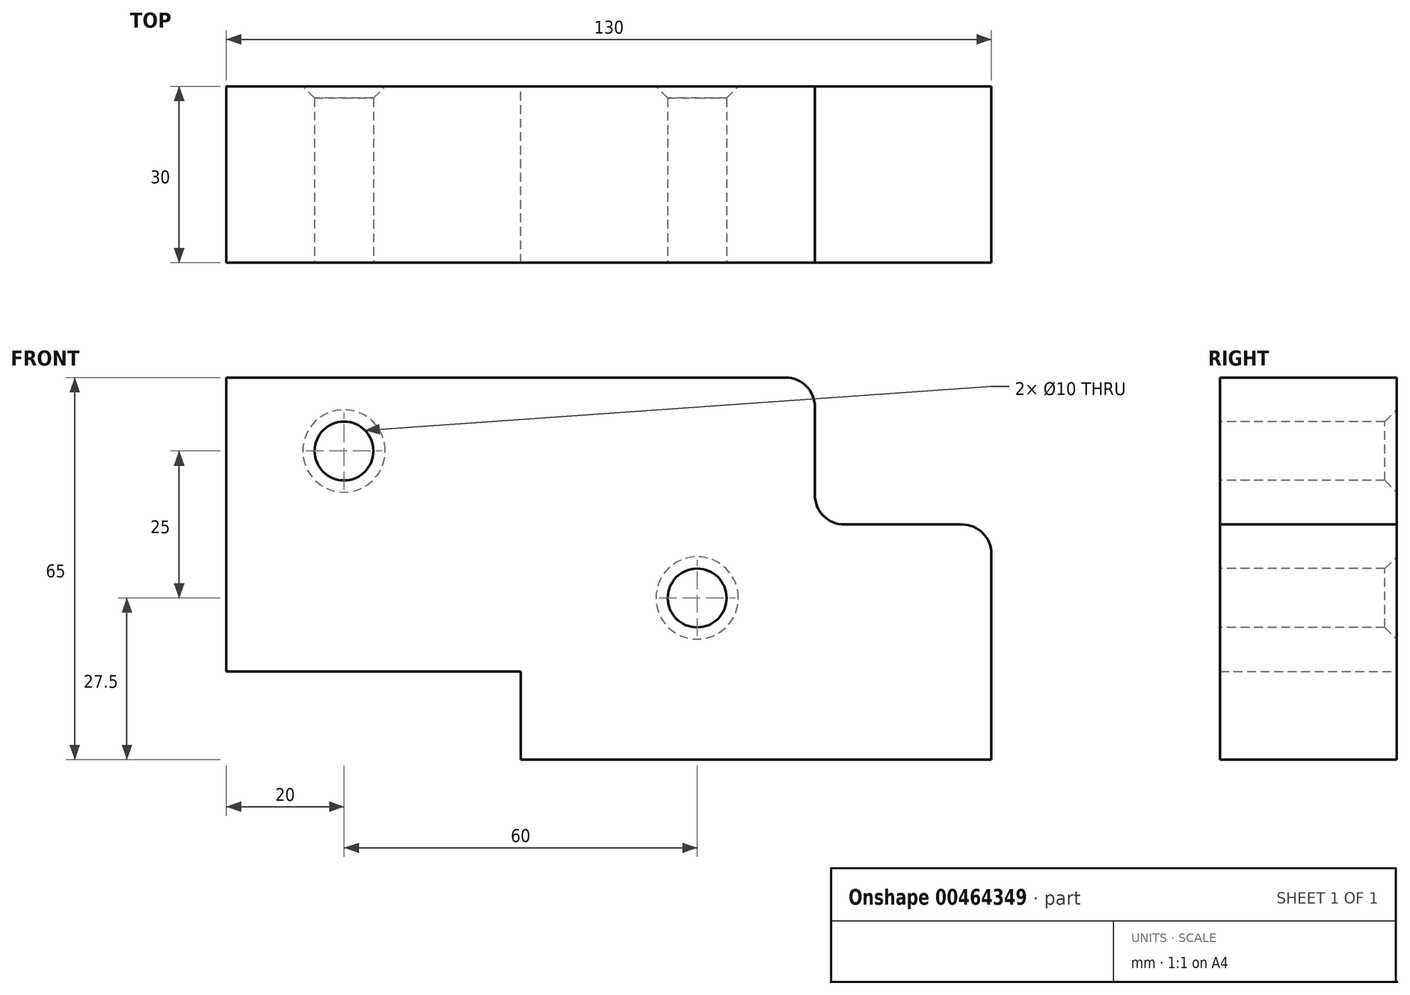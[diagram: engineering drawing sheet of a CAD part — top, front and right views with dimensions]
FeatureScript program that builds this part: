
annotation { "Feature Type Name" : "Feature", "Feature Type Description" : "" }
export const myFeature = defineFeature(function(context is Context, id is Id, definition is map)
    precondition{}
    {
        {
            var Q0;
            Q0=qCreatedBy(makeId("Front.planeOp"),FACE);
            var sketch = newSketch(context, id + "F0", { "sketchPlane" : qUnion([Q0])});
            skLineSegment(sketch, "E0.bottom", {"start": v(-50, 25) * mm, "end": v(50, 25) * mm});
            skLineSegment(sketch, "E0.top", {"start": v(-50, -25) * mm, "end": v(0, -25) * mm});
            skLineSegment(sketch, "E0.left", {"start": v(-50, 25) * mm, "end": v(-50, -25) * mm});
            skLineSegment(sketch, "E0.right", {"start": v(50, 25) * mm, "end": v(50, 0) * mm});
            skPoint(sketch, "E0.middle", {"position": v(0, 0) * mm});
            skLineSegment(sketch, "E1", {"start": v(0, -25) * mm, "end": v(0, -40) * mm});
            skPoint(sketch, "E1.endSnap0", {"position": v(0, -25) * mm});
            skLineSegment(sketch, "E2", {"start": v(0, -40) * mm, "end": v(80, -40) * mm});
            skLineSegment(sketch, "E3", {"start": v(80, -40) * mm, "end": v(80, 0) * mm});
            skLineSegment(sketch, "E4", {"start": v(80, 0) * mm, "end": v(50, 0) * mm});
            skPoint(sketch, "E5.orphan", {"position": v(50, -25) * mm});
            skSolve(sketch);
        }
        {
            var Q0;
            Q0=makeQuery(id+"F0.imprint","IMPRINT",FACE,{"disambiguationData":[TD([[makeQuery(id+"F0.imprint","IMPRINT",EDGE,{"derivedFrom":sQuery(id+"F0.wireOp",EDGE,"E0.bottom")}),-1.0]])]});
            extrude(context, id + "F1", {"entities" : qUnion([Q0]), "endBound" : BoundingType.SYMMETRIC, "depth" : 30 * mm});
        }
        {
            var Q0;
            Q0=makeQuery(id+"F1.opExtrude","SWEPT_EDGE",EDGE,{"disambiguationData":[OSD([sQuery(id+"F0.wireOp",EDGE,"E0.right"),sQuery(id+"F0.wireOp",EDGE,"E4")])]});
            var Q1;
            Q1=makeQuery(id+"F1.opExtrude","SWEPT_EDGE",EDGE,{"disambiguationData":[OSD([sQuery(id+"F0.wireOp",EDGE,"E0.bottom"),sQuery(id+"F0.wireOp",EDGE,"E0.right")])]});
            var Q2;
            Q2=makeQuery(id+"F1.opExtrude","SWEPT_EDGE",EDGE,{"disambiguationData":[OSD([sQuery(id+"F0.wireOp",EDGE,"E3"),sQuery(id+"F0.wireOp",EDGE,"E4")])]});
            fillet(context, id + "F2", {"entities" : qUnion([Q0, Q1, Q2]), "radius" : 5 * mm, "tangentPropagation" : true, "allowEdgeOverflow" : false});
        }
        {
            var Q0;
            Q0=makeQuery(id+"F1.opExtrude","CAP_FACE",FACE,{"disambiguationData":[OSD([sQuery(id+"F0.wireOp",EDGE,"E0.bottom"),sQuery(id+"F0.wireOp",EDGE,"E0.top"),sQuery(id+"F0.wireOp",EDGE,"E0.left"),sQuery(id+"F0.wireOp",EDGE,"E0.right"),sQuery(id+"F0.wireOp",EDGE,"E1"),sQuery(id+"F0.wireOp",EDGE,"E2"),sQuery(id+"F0.wireOp",EDGE,"E3"),sQuery(id+"F0.wireOp",EDGE,"E4")])],"isStart":false});
            var sketch = newSketch(context, id + "F3", { "sketchPlane" : qUnion([Q0])});
            skCircle(sketch, "E6", {"center": v(-30, 12.5) * mm, "radius": 5 * mm});
            skLineSegment(sketch, "E7", {"start": v(0, 0) * mm, "end": v(-30, 12.5) * mm, "construction": true});
            skLineSegment(sketch, "E8", {"start": v(0, 0) * mm, "end": v(30, -12.5) * mm, "construction": true});
            skCircle(sketch, "E9", {"center": v(30, -12.5) * mm, "radius": 5 * mm});
            skSolve(sketch);
        }
        {
            var Q0;
            Q0=makeQuery(id+"F3.imprint","IMPRINT",FACE,{"disambiguationData":[TD([[makeQuery(id+"F3.imprint","IMPRINT",EDGE,{"derivedFrom":sQuery(id+"F3.wireOp",EDGE,"E6")}),1.0]])]});
            var Q1;
            Q1=makeQuery(id+"F3.imprint","IMPRINT",FACE,{"disambiguationData":[TD([[makeQuery(id+"F3.imprint","IMPRINT",EDGE,{"derivedFrom":sQuery(id+"F3.wireOp",EDGE,"E9")}),1.0]])]});
            extrude(context, id + "F4", {"entities" : qUnion([Q0, Q1]), "operationType" : NewBodyOperationType.REMOVE, "endBound" : BoundingType.THROUGH_ALL, "oppositeDirection" : true, "depth" : 25 * mm});
        }
        {
            var Q0;
            Q0=makeQuery(id+"F4.boolean.opBoolean","COPY",EDGE,{"derivedFrom":makeQuery(id+"F4.opExtrude","CAP_EDGE",EDGE,{"disambiguationData":[OSD([sQuery(id+"F3.wireOp",EDGE,"E6")])],"isStart":true})});
            var Q1;
            Q1=makeQuery(id+"F4.boolean.opBoolean","COPY",EDGE,{"derivedFrom":makeQuery(id+"F4.opExtrude","CAP_EDGE",EDGE,{"disambiguationData":[OSD([sQuery(id+"F3.wireOp",EDGE,"E9")])],"isStart":true})});
            var Q2;
            Q2=makeQuery(id+"F4.boolean.opBoolean","INTERSECT",EDGE,{"derivedFrom":[makeQuery(id+"F1.opExtrude","CAP_FACE",FACE,{"disambiguationData":[OSD([sQuery(id+"F0.wireOp",EDGE,"E0.bottom"),sQuery(id+"F0.wireOp",EDGE,"E0.top"),sQuery(id+"F0.wireOp",EDGE,"E0.left"),sQuery(id+"F0.wireOp",EDGE,"E0.right"),sQuery(id+"F0.wireOp",EDGE,"E1"),sQuery(id+"F0.wireOp",EDGE,"E2"),sQuery(id+"F0.wireOp",EDGE,"E3"),sQuery(id+"F0.wireOp",EDGE,"E4")])],"isStart":true}),makeQuery(id+"F4.opExtrude","SWEPT_FACE",FACE,{"disambiguationData":[OSD([sQuery(id+"F3.wireOp",EDGE,"E6")])]})]});
            var Q3;
            Q3=makeQuery(id+"F4.boolean.opBoolean","INTERSECT",EDGE,{"derivedFrom":[makeQuery(id+"F1.opExtrude","CAP_FACE",FACE,{"disambiguationData":[OSD([sQuery(id+"F0.wireOp",EDGE,"E0.bottom"),sQuery(id+"F0.wireOp",EDGE,"E0.top"),sQuery(id+"F0.wireOp",EDGE,"E0.left"),sQuery(id+"F0.wireOp",EDGE,"E0.right"),sQuery(id+"F0.wireOp",EDGE,"E1"),sQuery(id+"F0.wireOp",EDGE,"E2"),sQuery(id+"F0.wireOp",EDGE,"E3"),sQuery(id+"F0.wireOp",EDGE,"E4")])],"isStart":true}),makeQuery(id+"F4.opExtrude","SWEPT_FACE",FACE,{"disambiguationData":[OSD([sQuery(id+"F3.wireOp",EDGE,"E9")])]})]});
            chamfer(context, id + "F5", {"entities" : qUnion([Q0, Q1, Q2, Q3]), "width" : 2 * mm, "tangentPropagation" : true});
        }
    });
